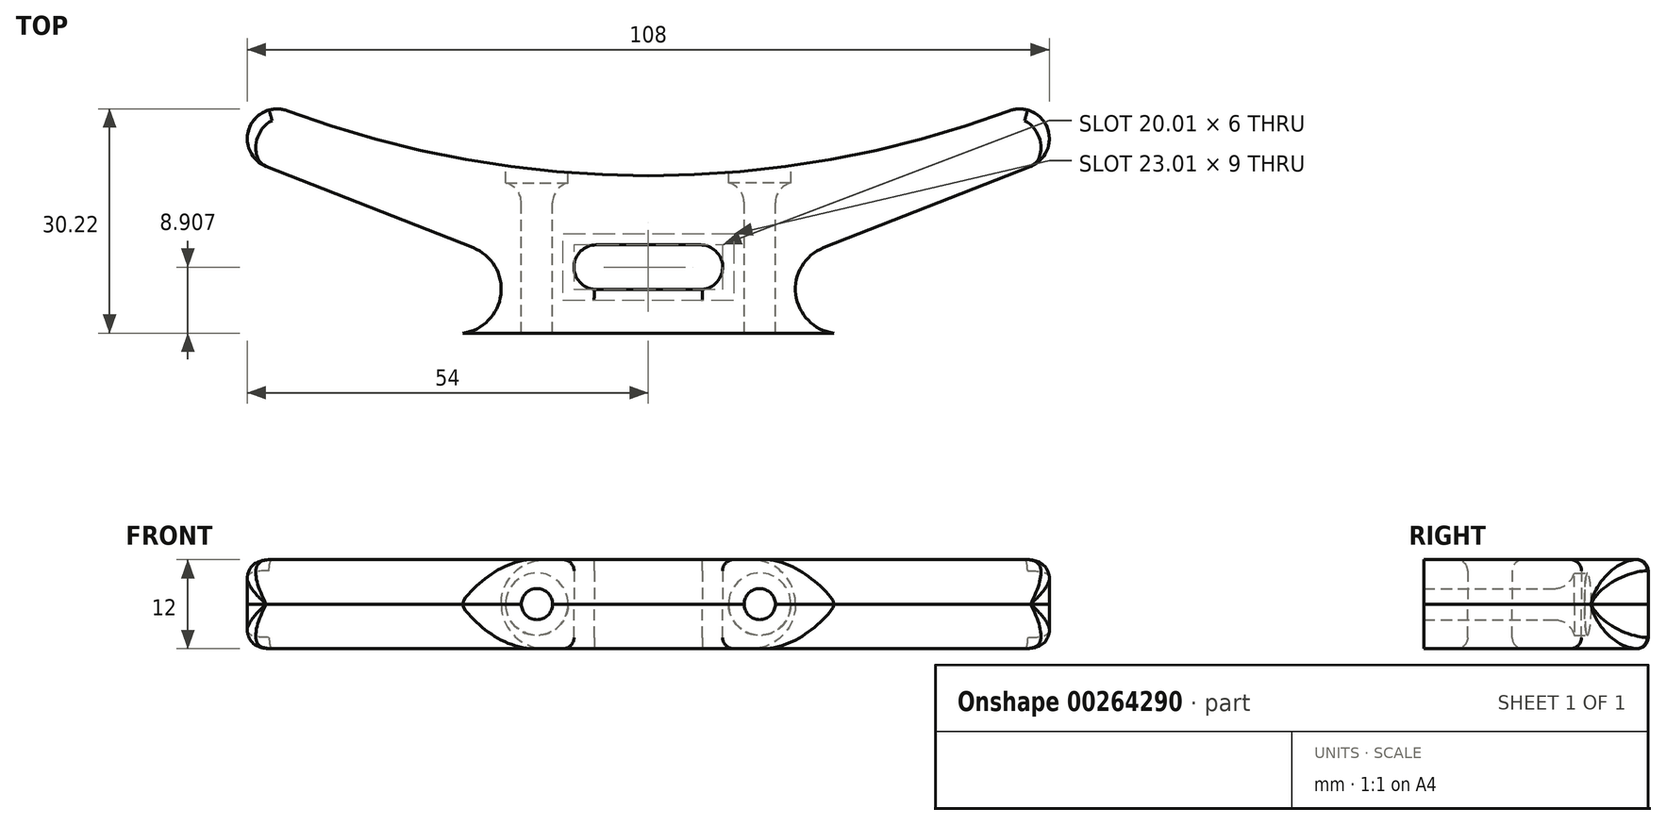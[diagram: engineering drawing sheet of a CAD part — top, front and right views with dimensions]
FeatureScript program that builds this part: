
annotation { "Feature Type Name" : "Feature", "Feature Type Description" : "" }
export const myFeature = defineFeature(function(context is Context, id is Id, definition is map)
    precondition{}
    {
        {
            var Q0;
            Q0=qCreatedBy(makeId("Top.planeOp"),FACE);
            var sketch = newSketch(context, id + "F0", { "sketchPlane" : qUnion([Q0])});
            skLineSegment(sketch, "E0", {"start": v(0, 0) * mm, "end": v(25, 0) * mm});
            skArc(sketch, "E1", {"start": v(25, 0) * mm, "mid": v(19.85, 5.23) * mm, "end": v(23.61, 11.53) * mm});
            skLineSegment(sketch, "E2", {"start": v(23.61, 11.53) * mm, "end": v(51.47, 22.5) * mm});
            skArc(sketch, "E3", {"start": v(51.47, 22.5) * mm, "mid": v(53.74, 27.65) * mm, "end": v(48.6, 29.97) * mm});
            skLineSegment(sketch, "E4", {"start": v(48.6, 29.97) * mm, "end": v(48.6, 29.97) * mm});
            skLineSegment(sketch, "E5", {"start": v(0, 11.9) * mm, "end": v(0, 0) * mm, "construction": true});
            skLineSegment(sketch, "E6.MirrorCS", {"start": v(0, 0) * mm, "end": v(-25, 0) * mm});
            skLineSegment(sketch, "E7.MirrorCS", {"start": v(-23.61, 11.53) * mm, "end": v(-51.47, 22.5) * mm});
            skArc(sketch, "E8.MirrorCS", {"start": v(-51.47, 22.5) * mm, "mid": v(-53.74, 27.65) * mm, "end": v(-48.6, 29.97) * mm});
            skArc(sketch, "E9.MirrorCS", {"start": v(-25, 0) * mm, "mid": v(-19.85, 5.23) * mm, "end": v(-23.61, 11.53) * mm});
            skLineSegment(sketch, "E10.MirrorCS", {"start": v(-48.6, 29.97) * mm, "end": v(-48.6, 29.97) * mm});
            skPoint(sketch, "E11.visualSharp", {"position": v(0, 11.9) * mm});
            skArc(sketch, "E11.filletArc", {"start": v(-48.6, 29.97) * mm, "mid": v(0, 21.23) * mm, "end": v(48.6, 29.97) * mm});
            skLineSegment(sketch, "E12.bottom", {"start": v(-7, 11.9) * mm, "end": v(7, 11.9) * mm});
            skLineSegment(sketch, "E12.top", {"start": v(-7.25, 5.9) * mm, "end": v(7.25, 5.9) * mm});
            skArc(sketch, "E13", {"start": v(-7, 11.9) * mm, "mid": v(-10, 9.03) * mm, "end": v(-7.25, 5.9) * mm});
            skArc(sketch, "E14", {"start": v(7, 11.9) * mm, "mid": v(10, 9.03) * mm, "end": v(7.25, 5.9) * mm});
            skSolve(sketch);
        }
        {
            var Q0;
            Q0=makeQuery(id+"F0.imprint","IMPRINT",FACE,{"disambiguationData":[TD([[makeQuery(id+"F0.imprint","IMPRINT",EDGE,{"derivedFrom":sQuery(id+"F0.wireOp",EDGE,"E0")}),1.0]])]});
            extrude(context, id + "F1", {"entities" : qUnion([Q0]), "depth" : 6 * mm});
        }
        {
            var Q0;
            Q0=makeQuery(id+"F1.opExtrude","CAP_EDGE",EDGE,{"disambiguationData":[OSD([sQuery(id+"F0.wireOp",EDGE,"E1")])],"isStart":false});
            var Q1;
            Q1=makeQuery(id+"F1.opExtrude","CAP_EDGE",EDGE,{"disambiguationData":[OSD([sQuery(id+"F0.wireOp",EDGE,"E2")])],"isStart":false});
            var Q2;
            Q2=makeQuery(id+"F1.opExtrude","CAP_EDGE",EDGE,{"disambiguationData":[OSD([sQuery(id+"F0.wireOp",EDGE,"E9.MirrorCS")])],"isStart":false});
            var Q3;
            Q3=makeQuery(id+"F1.opExtrude","CAP_EDGE",EDGE,{"disambiguationData":[OSD([sQuery(id+"F0.wireOp",EDGE,"E7.MirrorCS")])],"isStart":false});
            fillet(context, id + "F2", {"entities" : qUnion([Q0, Q1, Q2, Q3]), "radius" : 6 * mm, "allowEdgeOverflow" : false});
        }
        {
            var Q0;
            Q0=makeQuery(id+"F1.opExtrude","CAP_EDGE",EDGE,{"disambiguationData":[OSD([sQuery(id+"F0.wireOp",EDGE,"E8.MirrorCS")])],"isStart":false});
            var Q1;
            Q1=makeQuery(id+"F1.opExtrude","CAP_EDGE",EDGE,{"disambiguationData":[OSD([sQuery(id+"F0.wireOp",EDGE,"E11.filletArc")])],"isStart":false});
            var Q2;
            Q2=makeQuery(id+"F1.opExtrude","CAP_EDGE",EDGE,{"disambiguationData":[OSD([sQuery(id+"F0.wireOp",EDGE,"E3")])],"isStart":false});
            var Q3;
            Q3=makeQuery(id+"F1.opExtrude","CAP_EDGE",EDGE,{"disambiguationData":[OSD([sQuery(id+"F0.wireOp",EDGE,"E14")])],"isStart":false});
            var Q4;
            Q4=makeQuery(id+"F1.opExtrude","CAP_EDGE",EDGE,{"disambiguationData":[OSD([sQuery(id+"F0.wireOp",EDGE,"E12.top")])],"isStart":false});
            fillet(context, id + "F3", {"entities" : qUnion([Q0, Q1, Q2, Q3, Q4]), "radius" : 1.5 * mm, "tangentPropagation" : true, "allowEdgeOverflow" : false});
        }
        {
            var Q0;
            Q0=makeQuery(id+"F1.opExtrude","SWEPT_BODY",BODY,{"disambiguationData":[OSD([sQuery(id+"F0.wireOp",EDGE,"E0"),sQuery(id+"F0.wireOp",EDGE,"986a92c0-bd5c-40db-93ed-fe08f463a48d"),sQuery(id+"F0.wireOp",EDGE,"E1"),sQuery(id+"F0.wireOp",EDGE,"E2"),sQuery(id+"F0.wireOp",EDGE,"E3"),sQuery(id+"F0.wireOp",EDGE,"E4"),sQuery(id+"F0.wireOp",EDGE,"6bb3b665-96de-4027-b85e-78878124d9a30.MirrorCS"),sQuery(id+"F0.wireOp",EDGE,"E6.MirrorCS"),sQuery(id+"F0.wireOp",EDGE,"E7.MirrorCS"),sQuery(id+"F0.wireOp",EDGE,"E8.MirrorCS"),sQuery(id+"F0.wireOp",EDGE,"E9.MirrorCS"),sQuery(id+"F0.wireOp",EDGE,"E10.MirrorCS"),sQuery(id+"F0.wireOp",EDGE,"E11.filletArc")])]});
            var Q1;
            Q1=makeQuery(id+"F1.opExtrude","CAP_FACE",FACE,{"disambiguationData":[OSD([sQuery(id+"F0.wireOp",EDGE,"E0"),sQuery(id+"F0.wireOp",EDGE,"986a92c0-bd5c-40db-93ed-fe08f463a48d"),sQuery(id+"F0.wireOp",EDGE,"E1"),sQuery(id+"F0.wireOp",EDGE,"E2"),sQuery(id+"F0.wireOp",EDGE,"E3"),sQuery(id+"F0.wireOp",EDGE,"E4"),sQuery(id+"F0.wireOp",EDGE,"6bb3b665-96de-4027-b85e-78878124d9a30.MirrorCS"),sQuery(id+"F0.wireOp",EDGE,"E6.MirrorCS"),sQuery(id+"F0.wireOp",EDGE,"E7.MirrorCS"),sQuery(id+"F0.wireOp",EDGE,"E8.MirrorCS"),sQuery(id+"F0.wireOp",EDGE,"E9.MirrorCS"),sQuery(id+"F0.wireOp",EDGE,"E10.MirrorCS"),sQuery(id+"F0.wireOp",EDGE,"E11.filletArc")])],"isStart":true});
            mirror(context, id + "F4", {"entities" : qUnion([Q0]), "mirrorPlane" : qUnion([Q1])});
        }
        {
            var Q0;
            Q0=qCreatedBy(makeId("Top.planeOp"),FACE);
            var sketch = newSketch(context, id + "F5", { "sketchPlane" : qUnion([Q0])});
            skLineSegment(sketch, "E15", {"start": v(0, 0) * mm, "end": v(15, 0) * mm, "construction": true});
            skLineSegment(sketch, "E16", {"start": v(15, 0) * mm, "end": v(15, 23.24) * mm, "construction": true});
            skLineSegment(sketch, "E17", {"start": v(15, 23.24) * mm, "end": v(19.2, 23.24) * mm});
            skLineSegment(sketch, "E18", {"start": v(19.2, 23.24) * mm, "end": v(19.2, 20.24) * mm});
            skArc(sketch, "E19", {"start": v(19.2, 20.24) * mm, "mid": v(17.69, 19.26) * mm, "end": v(17.1, 17.56) * mm});
            skLineSegment(sketch, "E20", {"start": v(17.1, 17.56) * mm, "end": v(17.1, -4.12) * mm});
            skLineSegment(sketch, "E21", {"start": v(17.1, -4.12) * mm, "end": v(15, -4.12) * mm});
            skLineSegment(sketch, "E22", {"start": v(15, -4.12) * mm, "end": v(15, 23.24) * mm});
            skLineSegment(sketch, "E23", {"start": v(0, 0) * mm, "end": v(0, 19.09) * mm, "construction": true});
            skPoint(sketch, "E23.endSnap0", {"position": v(0, 19.96) * mm});
            skSolve(sketch);
        }
        {
            var Q0;
            {var subQ5=sQuery(id+"F5.wireOp",EDGE,"E19");Q0=makeQuery(id+"F5.imprint","IMPRINT",FACE,{"disambiguationData":[TD([[makeQuery(id+"F5.imprint","IMPRINT",EDGE,{"derivedFrom":subQ5}),-1.0]])]});}
            var Q1;
            {var subQ0=sQuery(id+"F5.wireOp",EDGE,"E17");Q1=makeQuery(id+"F5.imprint","IMPRINT",FACE,{"disambiguationData":[TD([[makeQuery(id+"F5.imprint","IMPRINT",EDGE,{"derivedFrom":subQ0}),-1.0]])]});}
            var Q2;
            Q2=sQuery(id+"F5.wireOp",EDGE,"E22");
            revolve(context, id + "F6", {"entities" : qUnion([Q0, Q1]), "axis" : qUnion([Q2]), "revolveType" : RevolveType.FULL, "oppositeDirection" : true});
        }
        {
            var Q0;
            Q0=makeQuery(id+"F6.opRevolve","SWEPT_BODY",BODY,{"disambiguationData":[OSD([sQuery(id+"F0.wireOp",EDGE,"E0"),sQuery(id+"F0.wireOp",EDGE,"E6.MirrorCS"),sQuery(id+"F5.wireOp",EDGE,"E17"),sQuery(id+"F5.wireOp",EDGE,"E18"),sQuery(id+"F5.wireOp",EDGE,"E19"),sQuery(id+"F5.wireOp",EDGE,"E20"),sQuery(id+"F5.wireOp",EDGE,"E22")])]});
            var Q1;
            Q1=qCreatedBy(makeId("Right.planeOp"),FACE);
            mirror(context, id + "F7", {"entities" : qUnion([Q0]), "mirrorPlane" : qUnion([Q1])});
        }
        {
            var Q0;
            Q0=makeQuery(id+"F6.opRevolve","SWEPT_BODY",BODY,{"disambiguationData":[OSD([sQuery(id+"F0.wireOp",EDGE,"E0"),sQuery(id+"F0.wireOp",EDGE,"E6.MirrorCS"),sQuery(id+"F5.wireOp",EDGE,"E17"),sQuery(id+"F5.wireOp",EDGE,"E18"),sQuery(id+"F5.wireOp",EDGE,"E19"),sQuery(id+"F5.wireOp",EDGE,"E20"),sQuery(id+"F5.wireOp",EDGE,"E22")])]});
            var Q1;
            Q1=makeQuery(id+"F7.opPattern","COPY",BODY,{"derivedFrom":makeQuery(id+"F6.opRevolve","SWEPT_BODY",BODY,{"disambiguationData":[OSD([sQuery(id+"F0.wireOp",EDGE,"E0"),sQuery(id+"F0.wireOp",EDGE,"E6.MirrorCS"),sQuery(id+"F5.wireOp",EDGE,"E17"),sQuery(id+"F5.wireOp",EDGE,"E18"),sQuery(id+"F5.wireOp",EDGE,"E19"),sQuery(id+"F5.wireOp",EDGE,"E20"),sQuery(id+"F5.wireOp",EDGE,"E22")])]}),"instanceName":"1"});
            var Q2;
            Q2=makeQuery(id+"F1.opExtrude","SWEPT_BODY",BODY,{"disambiguationData":[OSD([sQuery(id+"F0.wireOp",EDGE,"E0"),sQuery(id+"F0.wireOp",EDGE,"986a92c0-bd5c-40db-93ed-fe08f463a48d"),sQuery(id+"F0.wireOp",EDGE,"E1"),sQuery(id+"F0.wireOp",EDGE,"E2"),sQuery(id+"F0.wireOp",EDGE,"E3"),sQuery(id+"F0.wireOp",EDGE,"6bb3b665-96de-4027-b85e-78878124d9a30.MirrorCS"),sQuery(id+"F0.wireOp",EDGE,"E6.MirrorCS"),sQuery(id+"F0.wireOp",EDGE,"E7.MirrorCS"),sQuery(id+"F0.wireOp",EDGE,"E8.MirrorCS"),sQuery(id+"F0.wireOp",EDGE,"E9.MirrorCS"),sQuery(id+"F0.wireOp",EDGE,"E11.filletArc")])]});
            var Q3;
            Q3=makeQuery(id+"F4.opPattern","COPY",BODY,{"derivedFrom":makeQuery(id+"F1.opExtrude","SWEPT_BODY",BODY,{"disambiguationData":[OSD([sQuery(id+"F0.wireOp",EDGE,"E0"),sQuery(id+"F0.wireOp",EDGE,"986a92c0-bd5c-40db-93ed-fe08f463a48d"),sQuery(id+"F0.wireOp",EDGE,"E1"),sQuery(id+"F0.wireOp",EDGE,"E2"),sQuery(id+"F0.wireOp",EDGE,"E3"),sQuery(id+"F0.wireOp",EDGE,"6bb3b665-96de-4027-b85e-78878124d9a30.MirrorCS"),sQuery(id+"F0.wireOp",EDGE,"E6.MirrorCS"),sQuery(id+"F0.wireOp",EDGE,"E7.MirrorCS"),sQuery(id+"F0.wireOp",EDGE,"E8.MirrorCS"),sQuery(id+"F0.wireOp",EDGE,"E9.MirrorCS"),sQuery(id+"F0.wireOp",EDGE,"E11.filletArc")])]}),"instanceName":"1"});
            booleanBodies(context, id + "F8", {"operationType" : BooleanOperationType.SUBTRACTION, "tools" : qUnion([Q0, Q1]), "targets" : qUnion([Q2, Q3])});
        }
    });
